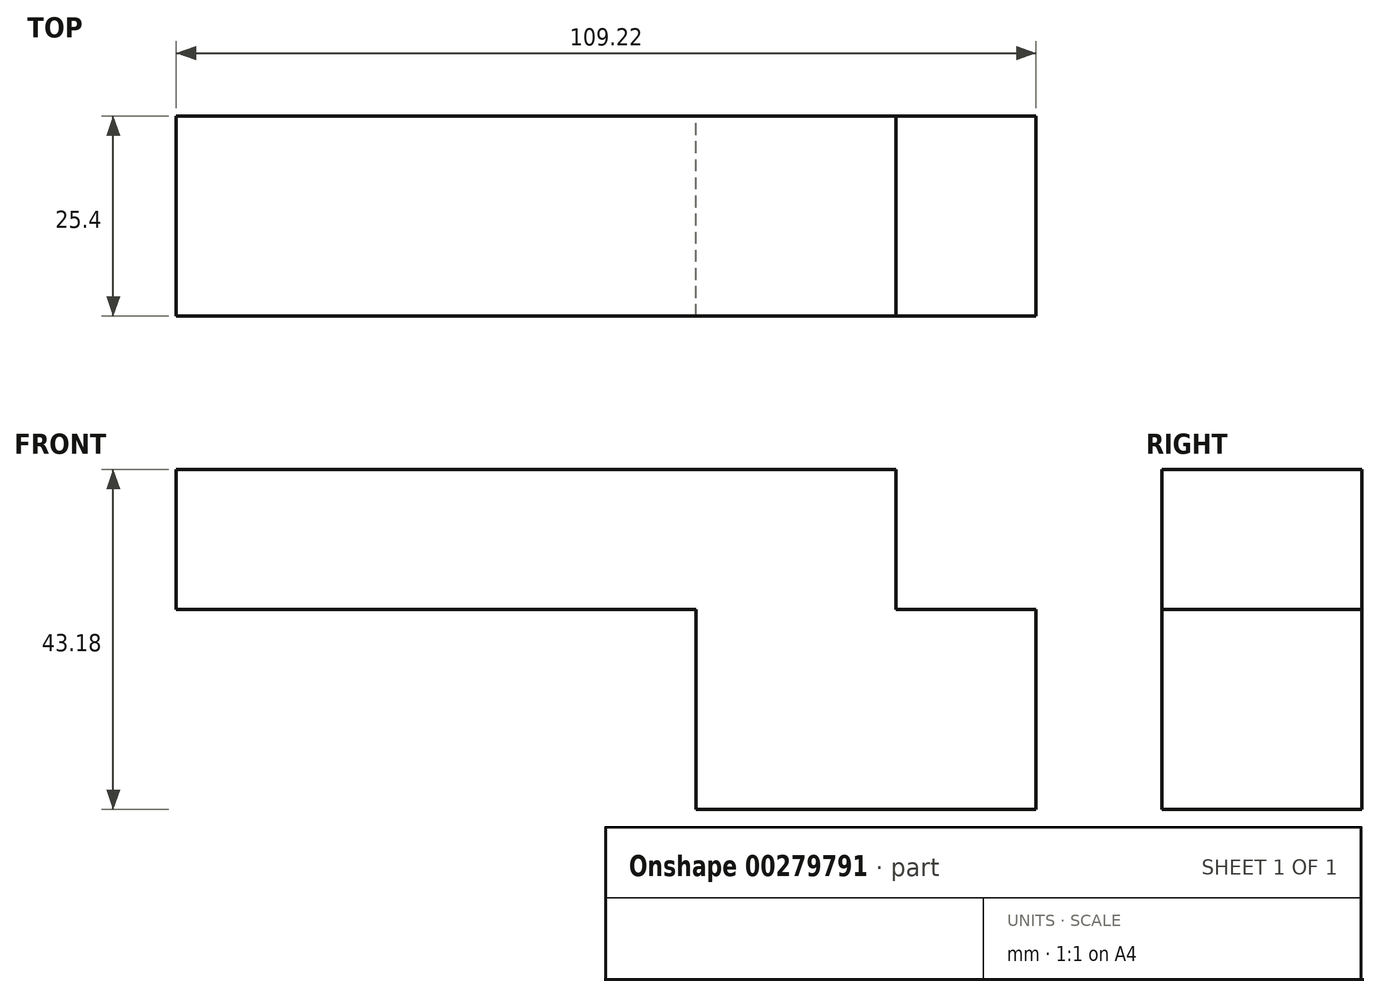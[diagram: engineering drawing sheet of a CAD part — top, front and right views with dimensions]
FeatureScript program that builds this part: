
annotation { "Feature Type Name" : "Feature", "Feature Type Description" : "" }
export const myFeature = defineFeature(function(context is Context, id is Id, definition is map)
    precondition{}
    {
        {
            var Q0;
            Q0=qCreatedBy(makeId("Top.planeOp"),FACE);
            var sketch = newSketch(context, id + "F0", { "sketchPlane" : qUnion([Q0])});
            skLineSegment(sketch, "E0.bottom", {"start": v(-60.7, 59.07) * mm, "end": v(30.73, 59.07) * mm});
            skLineSegment(sketch, "E0.top", {"start": v(-60.7, 33.67) * mm, "end": v(30.73, 33.67) * mm});
            skLineSegment(sketch, "E0.left", {"start": v(-60.7, 59.07) * mm, "end": v(-60.7, 33.67) * mm});
            skLineSegment(sketch, "E0.right", {"start": v(30.73, 59.07) * mm, "end": v(30.73, 33.67) * mm});
            skSolve(sketch);
        }
        {
            var Q0;
            Q0=makeQuery(id+"F0.imprint","IMPRINT",FACE,{"disambiguationData":[TD([[makeQuery(id+"F0.imprint","IMPRINT",EDGE,{"derivedFrom":sQuery(id+"F0.wireOp",EDGE,"E0.bottom")}),-1.0]])]});
            extrude(context, id + "F1", {"entities" : qUnion([Q0]), "depth" : 17.78 * mm});
        }
        {
            var Q0;
            Q0=makeQuery(id+"F1.opExtrude","CAP_FACE",FACE,{"disambiguationData":[OSD([sQuery(id+"F0.wireOp",EDGE,"E0.bottom"),sQuery(id+"F0.wireOp",EDGE,"E0.top"),sQuery(id+"F0.wireOp",EDGE,"E0.left"),sQuery(id+"F0.wireOp",EDGE,"E0.right")])],"isStart":true});
            var sketch = newSketch(context, id + "F2", { "sketchPlane" : qUnion([Q0])});
            skLineSegment(sketch, "E1", {"start": v(5.33, -33.67) * mm, "end": v(5.33, -59.07) * mm});
            skSolve(sketch);
        }
        {
            var Q0;
            {var subQ0=sQuery(id+"F2.wireOp",EDGE,"E1");Q0=makeQuery(id+"F2.imprint","IMPRINT",FACE,{"disambiguationData":[TD([[makeQuery(id+"F2.imprint","IMPRINT",EDGE,{"derivedFrom":subQ0}),1.0]])]});}
            extrude(context, id + "F3", {"entities" : qUnion([Q0]), "operationType" : NewBodyOperationType.ADD, "depth" : 25.4 * mm});
        }
        {
            var Q0;
            {var subQ0=sQuery(id+"F0.wireOp",EDGE,"E0.right");Q0=makeQuery(id+"F3.boolean.opBoolean","MERGE",FACE,{"derivedFrom":[makeQuery(id+"F1.opExtrude","SWEPT_FACE",FACE,{"disambiguationData":[OSD([subQ0])]}),makeQuery(id+"F3.opExtrude","SWEPT_FACE",FACE,{"disambiguationData":[OSD([subQ0])]})]});}
            var sketch = newSketch(context, id + "F4", { "sketchPlane" : qUnion([Q0])});
            skLineSegment(sketch, "E2", {"start": v(33.67, 0) * mm, "end": v(59.07, 0) * mm});
            skSolve(sketch);
        }
        {
            var Q0;
            {var subQ0=sQuery(id+"F4.wireOp",EDGE,"E2");Q0=makeQuery(id+"F4.imprint","IMPRINT",FACE,{"disambiguationData":[TD([[makeQuery(id+"F4.imprint","IMPRINT",EDGE,{"derivedFrom":subQ0}),-1.0]])]});}
            extrude(context, id + "F5", {"entities" : qUnion([Q0]), "operationType" : NewBodyOperationType.ADD, "depth" : 17.78 * mm});
        }
    });
